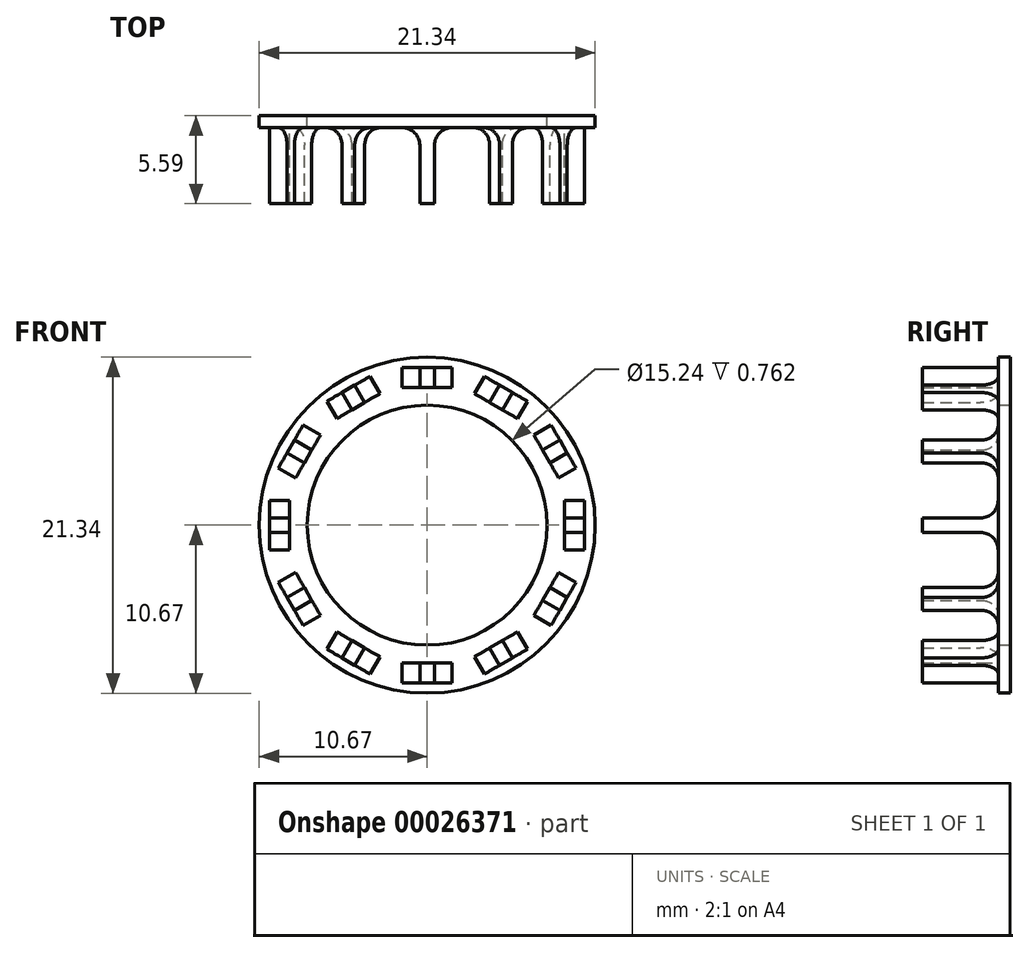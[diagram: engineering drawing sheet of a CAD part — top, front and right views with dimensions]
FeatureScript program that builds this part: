
annotation { "Feature Type Name" : "Feature", "Feature Type Description" : "" }
export const myFeature = defineFeature(function(context is Context, id is Id, definition is map)
    precondition{}
    {
        {
            var Q0;
            Q0=qCreatedBy(makeId("Front.planeOp"),FACE);
            var sketch = newSketch(context, id + "F0", { "sketchPlane" : qUnion([Q0])});
            skCircle(sketch, "E0", {"center": v(0, 0) * mm, "radius": 10.67 * mm});
            skCircle(sketch, "E1", {"center": v(0, 0) * mm, "radius": 7.62 * mm});
            skSolve(sketch);
        }
        {
            var Q0;
            Q0=makeQuery(id+"F0.imprint","IMPRINT",FACE,{"disambiguationData":[TD([[makeQuery(id+"F0.imprint","IMPRINT",EDGE,{"derivedFrom":sQuery(id+"F0.wireOp",EDGE,"E0")}),1.0]])]});
            extrude(context, id + "F1", {"entities" : qUnion([Q0]), "depth" : 0.76 * mm});
        }
        {
            var Q0;
            Q0=qCreatedBy(makeId("Right.planeOp"),FACE);
            var sketch = newSketch(context, id + "F2", { "sketchPlane" : qUnion([Q0])});
            skLineSegment(sketch, "E2.0", {"start": v(-0.76, 1.58) * mm, "end": v(-0.76, 10.67) * mm, "construction": true});
            skLineSegment(sketch, "E3.bottom", {"start": v(-1.88, -0.46) * mm, "end": v(-5.59, -0.46) * mm});
            skLineSegment(sketch, "E3.top", {"start": v(-1.88, 0.46) * mm, "end": v(-5.59, 0.46) * mm});
            skLineSegment(sketch, "E3.right", {"start": v(-5.59, -0.46) * mm, "end": v(-5.59, 0.46) * mm});
            skPoint(sketch, "E4.newPointB", {"position": v(-0.76, -10.67) * mm});
            skArc(sketch, "E4.filletArc", {"start": v(-1.88, 0.46) * mm, "mid": v(-1.09, 0.8) * mm, "end": v(-0.76, 1.58) * mm});
            skArc(sketch, "E5.MirrorCS", {"start": v(-1.88, -0.46) * mm, "mid": v(-1.09, -0.8) * mm, "end": v(-0.76, -1.58) * mm});
            skLineSegment(sketch, "E6", {"start": v(-0.76, -1.58) * mm, "end": v(-0.76, 1.58) * mm});
            skLineSegment(sketch, "E7", {"start": v(0, 0) * mm, "end": v(-17.46, 0) * mm, "construction": true});
            skSolve(sketch);
        }
        {
            var Q0;
            Q0=makeQuery(id+"F2.imprint","IMPRINT",FACE,{"disambiguationData":[TD([[makeQuery(id+"F2.imprint","IMPRINT",EDGE,{"derivedFrom":sQuery(id+"F2.wireOp",EDGE,"E3.bottom")}),-1.0]])]});
            extrude(context, id + "F3", {"entities" : qUnion([Q0]), "depth" : 25.4 * mm});
        }
        {
            var Q0;
            Q0=makeQuery(id+"F1.opExtrude","CAP_FACE",FACE,{"disambiguationData":[OSD([sQuery(id+"F0.wireOp",EDGE,"E0"),sQuery(id+"F0.wireOp",EDGE,"E1")])],"isStart":false});
            var sketch = newSketch(context, id + "F4", { "sketchPlane" : qUnion([Q0])});
            skLineSegment(sketch, "E8.bottom", {"start": v(8.73, -2.03) * mm, "end": v(10, -2.03) * mm});
            skLineSegment(sketch, "E8.top", {"start": v(8.73, 1.76) * mm, "end": v(10, 1.76) * mm});
            skLineSegment(sketch, "E8.left", {"start": v(8.73, -2.03) * mm, "end": v(8.73, 1.76) * mm});
            skLineSegment(sketch, "E8.right", {"start": v(10, -2.03) * mm, "end": v(10, 1.76) * mm});
            skArc(sketch, "E9.0", {"start": v(10.66, 0.46) * mm, "mid": v(-10.67, 0) * mm, "end": v(10.66, -0.46) * mm, "construction": true});
            skLineSegment(sketch, "E10.bottom", {"start": v(-1.58, -13.33) * mm, "end": v(26.4, -13.33) * mm});
            skLineSegment(sketch, "E10.top", {"start": v(-1.58, 7.84) * mm, "end": v(26.4, 7.84) * mm});
            skLineSegment(sketch, "E10.left", {"start": v(-1.58, -13.33) * mm, "end": v(-1.58, 7.84) * mm});
            skLineSegment(sketch, "E10.right", {"start": v(26.4, -13.33) * mm, "end": v(26.4, 7.84) * mm});
            skCircle(sketch, "E11", {"center": v(0, 0) * mm, "radius": 8.68 * mm});
            skSolve(sketch);
        }
        {
            var Q0;
            {var subQ1=sQuery(id+"F4.wireOp",EDGE,"E10.bottom");Q0=makeQuery(id+"F4.imprint","IMPRINT",FACE,{"disambiguationData":[TD([[makeQuery(id+"F4.imprint","IMPRINT",EDGE,{"derivedFrom":subQ1}),1.0]])]});}
            var Q1;
            Q1=makeQuery(id+"F4.imprint","IMPRINT",FACE,{"disambiguationData":[TD([[makeQuery(id+"F4.imprint","IMPRINT",EDGE,{"derivedFrom":sQuery(id+"F4.wireOp",EDGE,"E8.bottom")}),-1.0]])]});
            var Q2;
            {var subQ0=sQuery(id+"F4.wireOp",EDGE,"E10.left");var subQ1=makeQuery(id+"F1.opExtrude","CAP_EDGE",EDGE,{"disambiguationData":[OSD([sQuery(id+"F0.wireOp",EDGE,"E1")])],"isStart":false});var subQ2=makeQuery(id+"F4.imprint","INTERSECT",VERTEX,{"disambiguationData":[OD(0.0)],"derivedFrom":[subQ1,subQ0]});Q2=makeQuery(id+"F4.imprint","IMPRINT",FACE,{"disambiguationData":[TD([[makeQuery(id+"F4.imprint","IMPRINT",EDGE,{"disambiguationData":[TD([[subQ2,-1.0]])],"derivedFrom":subQ0}),-1.0]])]});}
            var Q3;
            {var subQ1=sQuery(id+"F4.wireOp",EDGE,"E10.top");var subQ3=sQuery(id+"F4.wireOp",EDGE,"E10.left");var subQ5=makeQuery(id+"F4.imprint","INTERSECT",VERTEX,{"derivedFrom":[subQ1,subQ3]});Q3=makeQuery(id+"F4.imprint","IMPRINT",FACE,{"disambiguationData":[TD([[makeQuery(id+"F4.imprint","IMPRINT",EDGE,{"disambiguationData":[TD([[subQ5,-1.0]])],"derivedFrom":subQ1}),-1.0]])]});}
            extrude(context, id + "F5", {"entities" : qUnion([Q0, Q1, Q2, Q3]), "operationType" : NewBodyOperationType.REMOVE, "depth" : 25.4 * mm});
        }
        {
            var Q0;
            Q0=makeQuery(id+"F3.opExtrude","SWEPT_BODY",BODY,{"disambiguationData":[OSD([sQuery(id+"F2.wireOp",EDGE,"E3.bottom"),sQuery(id+"F2.wireOp",EDGE,"E3.top"),sQuery(id+"F2.wireOp",EDGE,"E3.right"),sQuery(id+"F2.wireOp",EDGE,"E4.filletArc"),sQuery(id+"F2.wireOp",EDGE,"E5.MirrorCS"),sQuery(id+"F2.wireOp",EDGE,"E6")])]});
            var Q1;
            Q1=sQuery(id+"F2.wireOp",EDGE,"E7");
            circularPattern(context, id + "F6", {"entities" : qUnion([Q0]), "axis" : qUnion([Q1]), "angle" : 30 * degree, "instanceCount" : 12});
        }
    });
